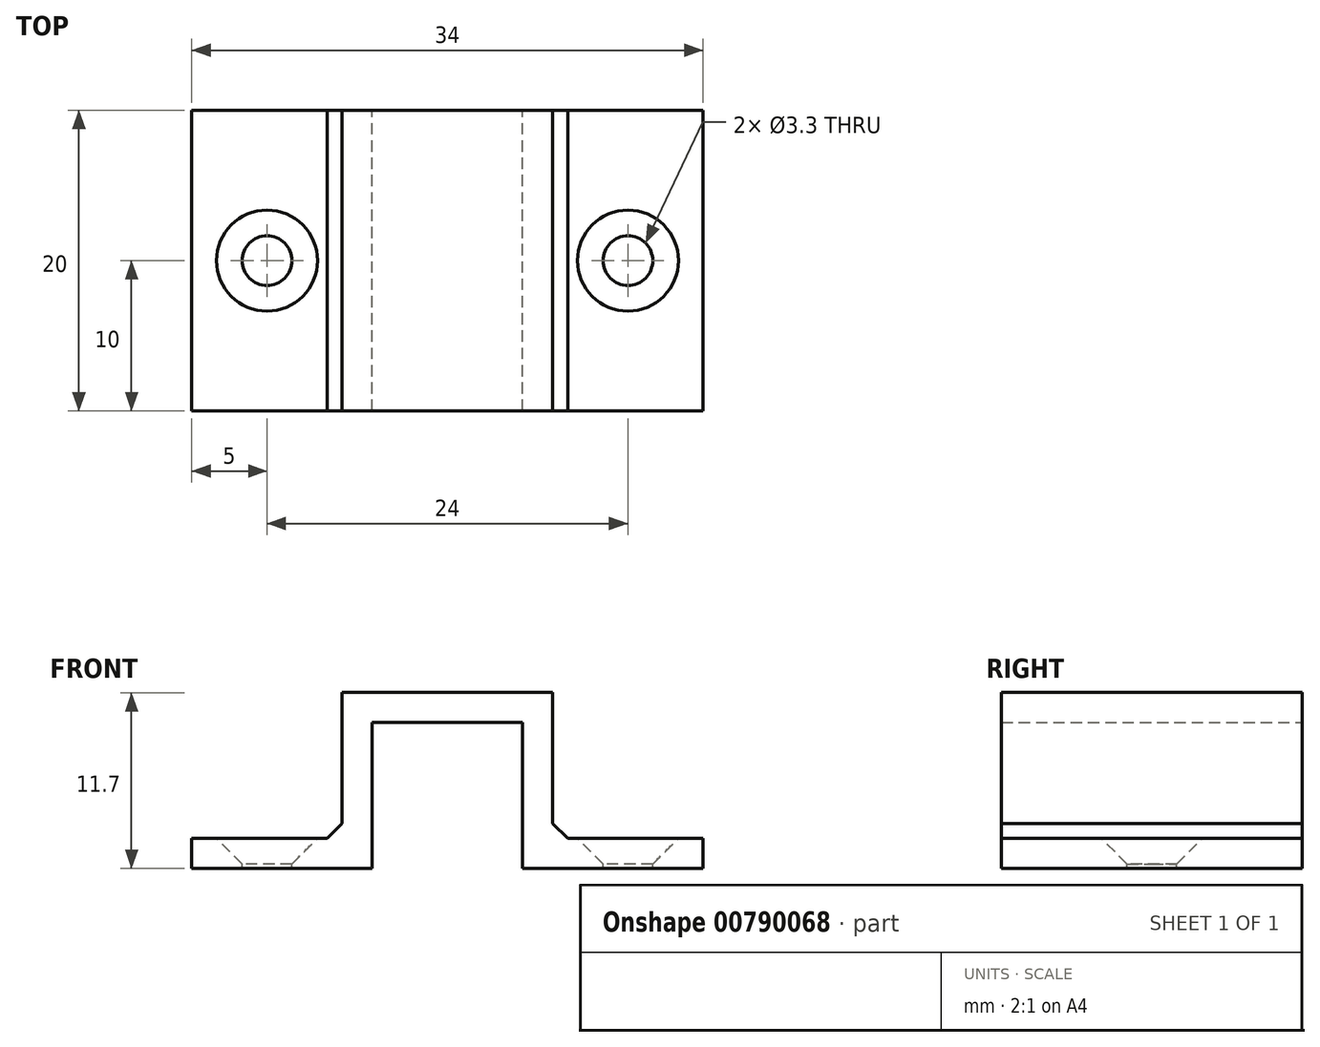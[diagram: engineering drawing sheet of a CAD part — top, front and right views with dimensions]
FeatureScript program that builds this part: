
annotation { "Feature Type Name" : "Feature", "Feature Type Description" : "" }
export const myFeature = defineFeature(function(context is Context, id is Id, definition is map)
    precondition{}
    {
        {
            var Q0;
            Q0=qCreatedBy(makeId("Front.planeOp"),FACE);
            var sketch = newSketch(context, id + "F0", { "sketchPlane" : qUnion([Q0])});
            skLineSegment(sketch, "E0", {"start": v(0, 0) * mm, "end": v(0, 2) * mm});
            skLineSegment(sketch, "E1", {"start": v(0, 2) * mm, "end": v(10, 2) * mm});
            skLineSegment(sketch, "E2", {"start": v(10, 2) * mm, "end": v(10, 11.7) * mm});
            skLineSegment(sketch, "E3", {"start": v(10, 11.7) * mm, "end": v(24, 11.7) * mm});
            skLineSegment(sketch, "E4", {"start": v(24, 11.7) * mm, "end": v(24, 2) * mm});
            skLineSegment(sketch, "E5", {"start": v(24, 2) * mm, "end": v(34, 2) * mm});
            skLineSegment(sketch, "E6", {"start": v(34, 2) * mm, "end": v(34, 0) * mm});
            skLineSegment(sketch, "E7", {"start": v(34, 0) * mm, "end": v(0, 0) * mm});
            skLineSegment(sketch, "E8", {"start": v(12, 0) * mm, "end": v(12, 9.7) * mm});
            skLineSegment(sketch, "E9", {"start": v(12, 9.7) * mm, "end": v(22, 9.7) * mm});
            skLineSegment(sketch, "E10", {"start": v(22, 9.7) * mm, "end": v(22, 0) * mm});
            skLineSegment(sketch, "E11", {"start": v(22, 0) * mm, "end": v(12, 0) * mm});
            skLineSegment(sketch, "E12", {"start": v(17, 11.7) * mm, "end": v(17, 0) * mm, "construction": true});
            skPoint(sketch, "E12.endSnap0", {"position": v(17, 0) * mm});
            skSolve(sketch);
        }
        {
            var Q0;
            {var subQ2=sQuery(id+"F0.wireOp",EDGE,"E0");Q0=makeQuery(id+"F0.imprint","IMPRINT",FACE,{"disambiguationData":[TD([[makeQuery(id+"F0.imprint","IMPRINT",EDGE,{"derivedFrom":subQ2}),-1.0]])]});}
            extrude(context, id + "F1", {"entities" : qUnion([Q0]), "depth" : 20 * mm, "offsetDistance" : 25 * mm});
        }
        {
            var Q0;
            Q0=makeQuery(id+"F1.opExtrude","SWEPT_FACE",FACE,{"disambiguationData":[OSD([sQuery(id+"F0.wireOp",EDGE,"E5")])]});
            var sketch = newSketch(context, id + "F2", { "sketchPlane" : qUnion([Q0])});
            skLineSegment(sketch, "E13", {"start": v(24, 0) * mm, "end": v(34, -20) * mm, "construction": true});
            skPoint(sketch, "E14", {"position": v(29, -10) * mm});
            skSolve(sketch);
        }
        {
            var Q0;
            Q0=makeQuery(id+"F1.opExtrude","SWEPT_FACE",FACE,{"disambiguationData":[OSD([sQuery(id+"F0.wireOp",EDGE,"E1")])]});
            var sketch = newSketch(context, id + "F3", { "sketchPlane" : qUnion([Q0])});
            skLineSegment(sketch, "E15", {"start": v(0, 0) * mm, "end": v(10, -20) * mm, "construction": true});
            skPoint(sketch, "E16", {"position": v(5, -10) * mm});
            skSolve(sketch);
        }
        {
            var Q0;
            Q0=sQuery(id+"F3.wireOp",VERTEX,"E16");
            var Q1;
            Q1=sQuery(id+"F2.wireOp",VERTEX,"E14");
            var Q2;
            Q2=makeQuery(id+"F1.opExtrude","SWEPT_BODY",BODY,{"disambiguationData":[OSD([sQuery(id+"F0.wireOp",EDGE,"E0"),sQuery(id+"F0.wireOp",EDGE,"E1"),sQuery(id+"F0.wireOp",EDGE,"E2"),sQuery(id+"F0.wireOp",EDGE,"E3"),sQuery(id+"F0.wireOp",EDGE,"E4"),sQuery(id+"F0.wireOp",EDGE,"E5"),sQuery(id+"F0.wireOp",EDGE,"E6"),sQuery(id+"F0.wireOp",EDGE,"E7"),sQuery(id+"F0.wireOp",EDGE,"E8"),sQuery(id+"F0.wireOp",EDGE,"E9"),sQuery(id+"F0.wireOp",EDGE,"E10")])]});
            hole(context, id + "F4", {"style" : HoleStyle.C_SINK, "endStyle" : HoleEndStyle.THROUGH, "standardTappedOrClearance" : lookupTablePath({ "standard" : "ISO", "fit" : "Normal", "size" : "M3", "type" : "Clearance" }), "standardBlindInLast" : lookupTablePath({ "fit" : "Standard", "standard" : "ISO", "size" : "M3", "type" : "Clearance" }), "holeDiameter" : 3.3 * mm, "cSinkDiameter" : 6.72 * mm, "cSinkAngle" : 90 * degree, "majorDiameter" : 5 * mm, "isTappedThrough" : true, "tappedDepth" : 12 * mm, "tapClearance" : 3, "locations" : qUnion([Q0, Q1]), "scope" : qUnion([Q2])});
        }
        {
            var Q0;
            Q0=makeQuery(id+"F1.opExtrude","SWEPT_EDGE",EDGE,{"disambiguationData":[OSD([sQuery(id+"F0.wireOp",EDGE,"E4"),sQuery(id+"F0.wireOp",EDGE,"E5")])]});
            var Q1;
            Q1=makeQuery(id+"F1.opExtrude","SWEPT_EDGE",EDGE,{"disambiguationData":[OSD([sQuery(id+"F0.wireOp",EDGE,"E1"),sQuery(id+"F0.wireOp",EDGE,"E2")])]});
            chamfer(context, id + "F5", {"entities" : qUnion([Q0, Q1]), "width" : 1 * mm, "tangentPropagation" : true});
        }
    });
